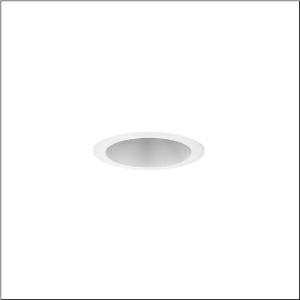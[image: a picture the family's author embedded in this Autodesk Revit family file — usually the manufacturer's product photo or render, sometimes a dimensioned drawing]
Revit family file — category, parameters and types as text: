
# Revit family: lunis_31_mini_51dn15de41
name_source: partatom
category: Lighting Fixtures
units: mm (PartAtom-declared; Revit-internal decimal feet)

## family parameters
Cut with Voids When Loaded = No
Host = Face
Light Source = No
Part Type = Normal
Room Calculation Point = No
Round Connector Dimension = Use Diameter
Shared = No

## types (1)
- Lunis 31 mini (1 x LED, 1040 lm, 8.3 W, 4000K)
    Apparent Load = 8 VA
    CIE Flux Codes = 93 98 100 100 100
    Color Rendering = 80
    Color Temperature = 4000K
    Default Elevation = 1800 mm
    Description = Lunis 31,  mini, downlight, light control with lens, light emission: direct distribution, LED rated luminous flux: 1.040lm, light colour: 840, mains connection: 220..240V, AC, 50/60Hz, housing, white, protection rating (complete): IP20, protection rating (on room side): IP54, insulation class (complete): insulation class II (safety insulation), certification: CE, packaging unit: 1 piece
    Height = 0 mm  [stored 0 ft]
    Lamp = 1 x LED
    Lamp Light Flux = 1040 lm
    Lamp Power = 8.3 W
    Lamp count = 1
    Length = 188 mm  [stored 0.616798 ft]
    Luminous efficacy = 125 lm/W
    Manufacturer = Siteco
    ModVariant = No
    Model = 51DN15DE41
    Mounting Place = Ceiling
    Mounting Type = Recessed
    Number of Poles = 1
    OnlyDefault = Yes
    Power Factor = 1
    Product Name = Lunis 31 mini
    Product group = downlight
    ProductGroupID = 400
    Protection Class = Protection class II
    Protection Degree = IP 20
    RLX_Detail_Level = 1
    RLX_Emergency_Light_Flux = 0 lm
    RLX_Emergency_Type = 0
    RLX_Emergency_Type_DB = No
    RlxData = <blob elided: 21801 chars, md5=cf09e792>
    Socket = socket
    Standby Power = 0 W
    System Light Flux = 1040 lm
    System Power = 8 W
    Type Comments = Product without accessories
    Type Image = l_1005624.jpg
    URL = http://relux.com
    VarID = ---
    Voltage = 0 V
    Weight = 0.00 kg
    Width = 0 mm  [stored 0 ft]

note: [stored X ft] marks values corroborated as IEEE doubles in the binary element streams (Revit-internal decimal feet)

## geometry (parser evidence)
native form markers: Blend x4, Sweep x12
no freeform markers — native parametric forms only
